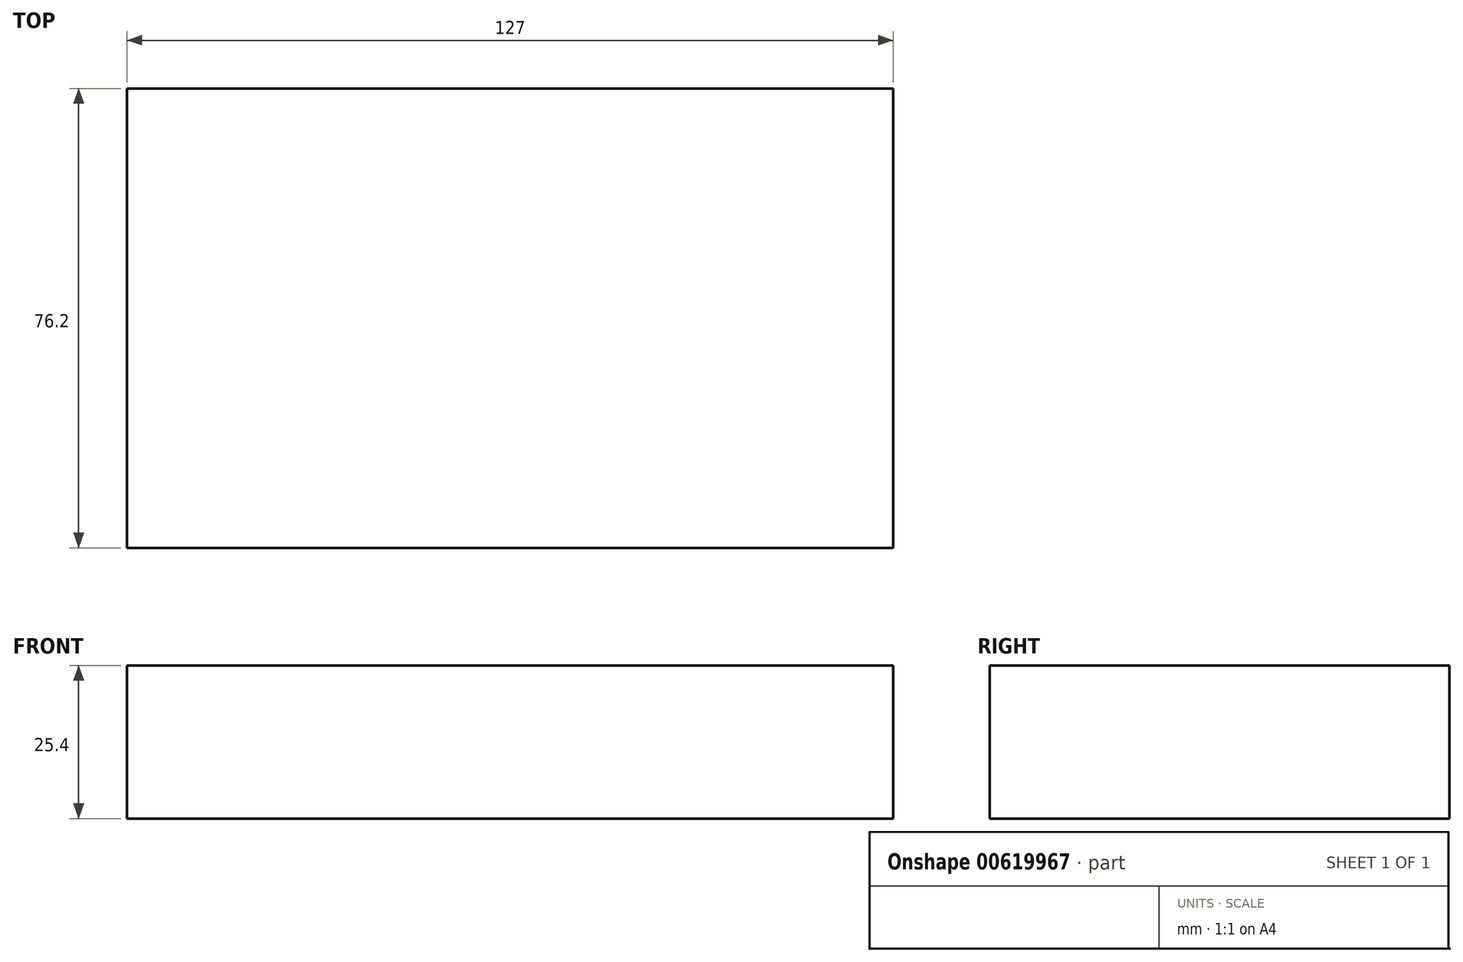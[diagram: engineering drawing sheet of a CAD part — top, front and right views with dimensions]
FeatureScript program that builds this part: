
annotation { "Feature Type Name" : "Feature", "Feature Type Description" : "" }
export const myFeature = defineFeature(function(context is Context, id is Id, definition is map)
    precondition{}
    {
        {
            var Q0;
            Q0=qCreatedBy(makeId("Top.planeOp"),FACE);
            var sketch = newSketch(context, id + "F0", { "sketchPlane" : qUnion([Q0])});
            skLineSegment(sketch, "E0.bottom", {"start": v(-52.85, 34) * mm, "end": v(74.15, 34) * mm});
            skLineSegment(sketch, "E0.top", {"start": v(-52.85, -42.2) * mm, "end": v(74.15, -42.2) * mm});
            skLineSegment(sketch, "E0.left", {"start": v(-52.85, 34) * mm, "end": v(-52.85, -42.2) * mm});
            skLineSegment(sketch, "E0.right", {"start": v(74.15, 34) * mm, "end": v(74.15, -42.2) * mm});
            skSolve(sketch);
        }
        {
            var Q0;
            Q0=makeQuery(id+"F0.imprint","IMPRINT",FACE,{"disambiguationData":[TD([[makeQuery(id+"F0.imprint","IMPRINT",EDGE,{"derivedFrom":sQuery(id+"F0.wireOp",EDGE,"E0.bottom")}),-1.0]])]});
            extrude(context, id + "F1", {"entities" : qUnion([Q0]), "endBound" : BoundingType.SYMMETRIC, "depth" : 25.4 * mm, "offsetDistance" : 25.4 * mm});
        }
    });
